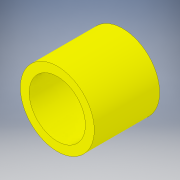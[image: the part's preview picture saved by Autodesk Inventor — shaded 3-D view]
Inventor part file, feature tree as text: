
AUTODESK INVENTOR PART (.ipt)
format: ipt  version: 2018 (Build 220112000, 112)  size: 110,592 bytes
history: native  units: in
note: dims shown in document units (in); Inventor stores cm internally (conversion verified against a paired STEP export)
features: extrude x1, sketch x1
ambient origin geometry x8: Origin, YZ Plane, XZ Plane, XY Plane, X Axis, Y Axis, Z Axis, Center Point
bodies: Solid1 (feature_tree)
feature tree (2):
  extrude  "Extrusion1"  Depth=1.163in
  sketch  "Sketch1"  dims[d0=1.315in d1=1.0in d2=1.163in d3=0.0in]
